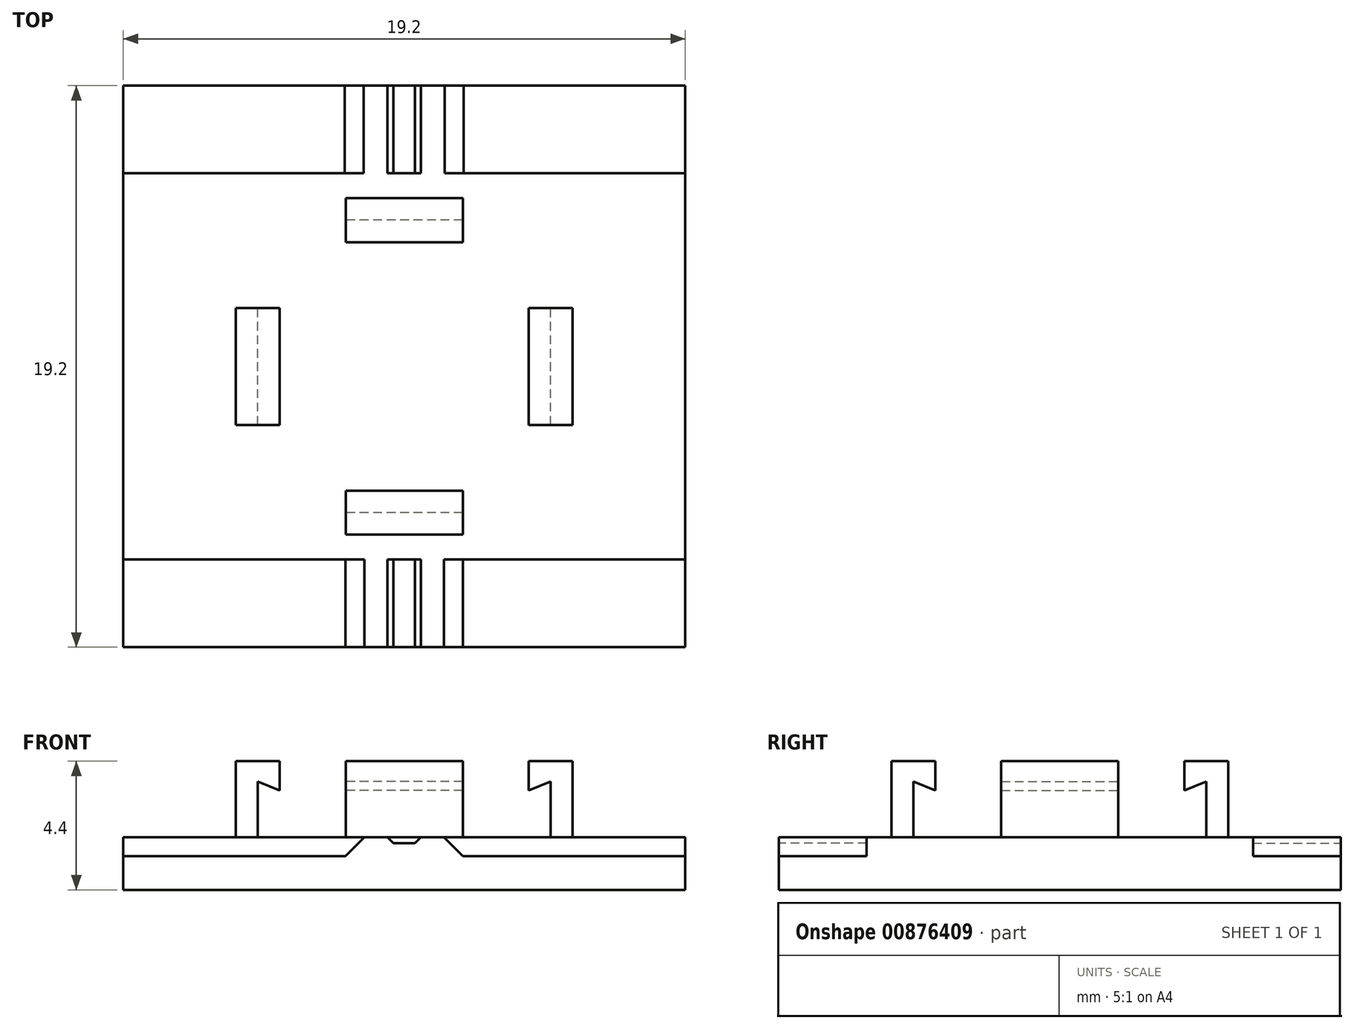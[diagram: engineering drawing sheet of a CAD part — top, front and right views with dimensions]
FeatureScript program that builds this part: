
annotation { "Feature Type Name" : "Feature", "Feature Type Description" : "" }
export const myFeature = defineFeature(function(context is Context, id is Id, definition is map)
    precondition{}
    {
        {
            var Q0;
            Q0=qCreatedBy(makeId("Top.planeOp"),FACE);
            var sketch = newSketch(context, id + "F0", { "sketchPlane" : qUnion([Q0])});
            skLineSegment(sketch, "E0.bottom", {"start": v(-9.6, 9.6) * mm, "end": v(9.6, 9.6) * mm});
            skLineSegment(sketch, "E0.top", {"start": v(-9.6, -9.6) * mm, "end": v(9.6, -9.6) * mm});
            skLineSegment(sketch, "E0.left", {"start": v(-9.6, 9.6) * mm, "end": v(-9.6, -9.6) * mm});
            skLineSegment(sketch, "E0.right", {"start": v(9.6, 9.6) * mm, "end": v(9.6, -9.6) * mm});
            skSolve(sketch);
        }
        {
            var Q0;
            Q0=makeQuery(id+"F0.imprint","IMPRINT",FACE,{"disambiguationData":[TD([[makeQuery(id+"F0.imprint","IMPRINT",EDGE,{"derivedFrom":sQuery(id+"F0.wireOp",EDGE,"E0.bottom")}),-1.0]])]});
            extrude(context, id + "F1", {"entities" : qUnion([Q0]), "depth" : 1.8 * mm, "offsetDistance" : 25 * mm});
        }
        {
            var Q0;
            Q0=makeQuery(id+"F1.opExtrude","SWEPT_FACE",FACE,{"disambiguationData":[OSD([sQuery(id+"F0.wireOp",EDGE,"E0.top")])]});
            var sketch = newSketch(context, id + "F2", { "sketchPlane" : qUnion([Q0])});
            skLineSegment(sketch, "E1", {"start": v(-1.36, 1.8) * mm, "end": v(-2.01, 1.15) * mm});
            skLineSegment(sketch, "E2", {"start": v(-2.01, 1.15) * mm, "end": v(-9.6, 1.15) * mm});
            skLineSegment(sketch, "E3", {"start": v(-9.6, 1.15) * mm, "end": v(-9.6, 1.8) * mm});
            skLineSegment(sketch, "E4", {"start": v(-9.6, 1.8) * mm, "end": v(-1.36, 1.8) * mm});
            skLineSegment(sketch, "E5", {"start": v(1.36, 1.8) * mm, "end": v(2.01, 1.15) * mm});
            skLineSegment(sketch, "E6", {"start": v(2.01, 1.15) * mm, "end": v(9.6, 1.15) * mm});
            skLineSegment(sketch, "E7", {"start": v(9.6, 1.15) * mm, "end": v(9.6, 1.8) * mm});
            skLineSegment(sketch, "E8", {"start": v(9.6, 1.8) * mm, "end": v(1.36, 1.8) * mm});
            skLineSegment(sketch, "E9", {"start": v(-0.57, 1.8) * mm, "end": v(-0.37, 1.6) * mm});
            skLineSegment(sketch, "E10", {"start": v(-0.37, 1.6) * mm, "end": v(0.37, 1.6) * mm});
            skLineSegment(sketch, "E11", {"start": v(0.37, 1.6) * mm, "end": v(0.57, 1.8) * mm});
            skLineSegment(sketch, "E12", {"start": v(0.57, 1.8) * mm, "end": v(-0.57, 1.8) * mm});
            skSolve(sketch);
        }
        {
            var Q0;
            Q0=makeQuery(id+"F2.imprint","IMPRINT",FACE,{"disambiguationData":[TD([[makeQuery(id+"F2.imprint","IMPRINT",EDGE,{"derivedFrom":sQuery(id+"F2.wireOp",EDGE,"E1")}),-1.0]])]});
            var Q1;
            Q1=makeQuery(id+"F2.imprint","IMPRINT",FACE,{"disambiguationData":[TD([[makeQuery(id+"F2.imprint","IMPRINT",EDGE,{"derivedFrom":sQuery(id+"F2.wireOp",EDGE,"E9")}),1.0]])]});
            var Q2;
            Q2=makeQuery(id+"F2.imprint","IMPRINT",FACE,{"disambiguationData":[TD([[makeQuery(id+"F2.imprint","IMPRINT",EDGE,{"derivedFrom":sQuery(id+"F2.wireOp",EDGE,"E5")}),1.0]])]});
            extrude(context, id + "F3", {"entities" : qUnion([Q0, Q1, Q2]), "operationType" : NewBodyOperationType.REMOVE, "oppositeDirection" : true, "depth" : 3 * mm, "offsetDistance" : 25 * mm});
        }
        {
            var Q0;
            Q0=makeQuery(id+"F1.opExtrude","SWEPT_FACE",FACE,{"disambiguationData":[OSD([sQuery(id+"F0.wireOp",EDGE,"E0.bottom")])]});
            var sketch = newSketch(context, id + "F4", { "sketchPlane" : qUnion([Q0])});
            skLineSegment(sketch, "E13", {"start": v(-9.6, 1.15) * mm, "end": v(-2.03, 1.15) * mm});
            skLineSegment(sketch, "E14", {"start": v(-2.03, 1.15) * mm, "end": v(-1.38, 1.8) * mm});
            skLineSegment(sketch, "E15", {"start": v(-1.38, 1.8) * mm, "end": v(-9.6, 1.8) * mm});
            skLineSegment(sketch, "E16", {"start": v(-9.6, 1.8) * mm, "end": v(-9.6, 1.15) * mm});
            skLineSegment(sketch, "E17", {"start": v(1.38, 1.8) * mm, "end": v(9.6, 1.8) * mm});
            skLineSegment(sketch, "E18", {"start": v(9.6, 1.8) * mm, "end": v(9.6, 1.15) * mm});
            skLineSegment(sketch, "E19", {"start": v(9.6, 1.15) * mm, "end": v(2.03, 1.15) * mm});
            skLineSegment(sketch, "E20", {"start": v(2.03, 1.15) * mm, "end": v(1.38, 1.8) * mm});
            skLineSegment(sketch, "E21", {"start": v(-0.57, 1.8) * mm, "end": v(-0.37, 1.6) * mm});
            skLineSegment(sketch, "E22", {"start": v(-0.37, 1.6) * mm, "end": v(0.37, 1.6) * mm});
            skLineSegment(sketch, "E23", {"start": v(0.37, 1.6) * mm, "end": v(0.57, 1.8) * mm});
            skLineSegment(sketch, "E24", {"start": v(0.57, 1.8) * mm, "end": v(-0.57, 1.8) * mm});
            skSolve(sketch);
        }
        {
            var Q0;
            Q0=makeQuery(id+"F4.imprint","IMPRINT",FACE,{"disambiguationData":[TD([[makeQuery(id+"F4.imprint","IMPRINT",EDGE,{"derivedFrom":sQuery(id+"F4.wireOp",EDGE,"E13")}),1.0]])]});
            var Q1;
            Q1=makeQuery(id+"F4.imprint","IMPRINT",FACE,{"disambiguationData":[TD([[makeQuery(id+"F4.imprint","IMPRINT",EDGE,{"derivedFrom":sQuery(id+"F4.wireOp",EDGE,"E21")}),1.0]])]});
            var Q2;
            Q2=makeQuery(id+"F4.imprint","IMPRINT",FACE,{"disambiguationData":[TD([[makeQuery(id+"F4.imprint","IMPRINT",EDGE,{"derivedFrom":sQuery(id+"F4.wireOp",EDGE,"E17")}),1.0]])]});
            extrude(context, id + "F5", {"entities" : qUnion([Q0, Q1, Q2]), "operationType" : NewBodyOperationType.REMOVE, "oppositeDirection" : true, "depth" : 3 * mm, "offsetDistance" : 25 * mm});
        }
        {
            var Q0;
            Q0=qCreatedBy(makeId("Front.planeOp"),FACE);
            var sketch = newSketch(context, id + "F6", { "sketchPlane" : qUnion([Q0])});
            skLineSegment(sketch, "E25", {"start": v(-5.75, 0) * mm, "end": v(-5.75, 4.4) * mm});
            skLineSegment(sketch, "E26", {"start": v(-5.75, 4.4) * mm, "end": v(-4.25, 4.4) * mm});
            skLineSegment(sketch, "E27", {"start": v(-4.25, 4.4) * mm, "end": v(-4.25, 3.4) * mm});
            skLineSegment(sketch, "E28", {"start": v(-4.25, 3.4) * mm, "end": v(-5, 3.7) * mm});
            skLineSegment(sketch, "E29", {"start": v(-5, 3.7) * mm, "end": v(-5, 0) * mm});
            skLineSegment(sketch, "E30", {"start": v(-5, 0) * mm, "end": v(-5.75, 0) * mm});
            skLineSegment(sketch, "E31.MirrorCS", {"start": v(5, 3.7) * mm, "end": v(5, 0) * mm});
            skLineSegment(sketch, "E32.MirrorCS", {"start": v(4.25, 3.4) * mm, "end": v(5, 3.7) * mm});
            skLineSegment(sketch, "E33.MirrorCS", {"start": v(4.25, 4.4) * mm, "end": v(4.25, 3.4) * mm});
            skLineSegment(sketch, "E34.MirrorCS", {"start": v(5, 0) * mm, "end": v(5.75, 0) * mm});
            skLineSegment(sketch, "E35.MirrorCS", {"start": v(5.75, 0) * mm, "end": v(5.75, 4.4) * mm});
            skLineSegment(sketch, "E36.MirrorCS", {"start": v(5.75, 4.4) * mm, "end": v(4.25, 4.4) * mm});
            skSolve(sketch);
        }
        {
            var Q0;
            Q0=makeQuery(id+"F6.imprint","IMPRINT",FACE,{"disambiguationData":[TD([[makeQuery(id+"F6.imprint","IMPRINT",EDGE,{"derivedFrom":sQuery(id+"F6.wireOp",EDGE,"E25")}),-1.0]])]});
            var Q1;
            Q1=makeQuery(id+"F6.imprint","IMPRINT",FACE,{"disambiguationData":[TD([[makeQuery(id+"F6.imprint","IMPRINT",EDGE,{"derivedFrom":sQuery(id+"F6.wireOp",EDGE,"E31.MirrorCS")}),1.0]])]});
            extrude(context, id + "F7", {"entities" : qUnion([Q0, Q1]), "operationType" : NewBodyOperationType.ADD, "depth" : 2 * mm, "offsetDistance" : 25 * mm, "hasSecondDirection" : true, "secondDirectionOppositeDirection" : true, "secondDirectionDepth" : 2 * mm});
        }
        {
            var Q0;
            Q0=qCreatedBy(makeId("Right.planeOp"),FACE);
            var sketch = newSketch(context, id + "F8", { "sketchPlane" : qUnion([Q0])});
            skLineSegment(sketch, "E37", {"start": v(-5.75, 0) * mm, "end": v(-5.75, 4.4) * mm});
            skLineSegment(sketch, "E38", {"start": v(-5.75, 4.4) * mm, "end": v(-4.25, 4.4) * mm});
            skLineSegment(sketch, "E39", {"start": v(-4.25, 4.4) * mm, "end": v(-4.25, 3.4) * mm});
            skLineSegment(sketch, "E40", {"start": v(-4.25, 3.4) * mm, "end": v(-5, 3.7) * mm});
            skLineSegment(sketch, "E41", {"start": v(-5, 3.7) * mm, "end": v(-5, 0) * mm});
            skLineSegment(sketch, "E42", {"start": v(-5, 0) * mm, "end": v(-5.75, 0) * mm});
            skLineSegment(sketch, "E43.MirrorCS", {"start": v(4.25, 3.4) * mm, "end": v(5, 3.7) * mm});
            skLineSegment(sketch, "E44.MirrorCS", {"start": v(5, 3.7) * mm, "end": v(5, 0) * mm});
            skLineSegment(sketch, "E45.MirrorCS", {"start": v(5, 0) * mm, "end": v(5.75, 0) * mm});
            skLineSegment(sketch, "E46.MirrorCS", {"start": v(4.25, 4.4) * mm, "end": v(4.25, 3.4) * mm});
            skLineSegment(sketch, "E47.MirrorCS", {"start": v(5.75, 4.4) * mm, "end": v(4.25, 4.4) * mm});
            skLineSegment(sketch, "E48.MirrorCS", {"start": v(5.75, 0) * mm, "end": v(5.75, 4.4) * mm});
            skSolve(sketch);
        }
        {
            var Q0;
            Q0=makeQuery(id+"F8.imprint","IMPRINT",FACE,{"disambiguationData":[TD([[makeQuery(id+"F8.imprint","IMPRINT",EDGE,{"derivedFrom":sQuery(id+"F8.wireOp",EDGE,"E37")}),-1.0]])]});
            var Q1;
            Q1=makeQuery(id+"F8.imprint","IMPRINT",FACE,{"disambiguationData":[TD([[makeQuery(id+"F8.imprint","IMPRINT",EDGE,{"derivedFrom":sQuery(id+"F8.wireOp",EDGE,"E43.MirrorCS")}),1.0]])]});
            extrude(context, id + "F9", {"entities" : qUnion([Q0, Q1]), "operationType" : NewBodyOperationType.ADD, "depth" : 2 * mm, "offsetDistance" : 25 * mm, "hasSecondDirection" : true, "secondDirectionOppositeDirection" : true, "secondDirectionDepth" : 2 * mm});
        }
    });
